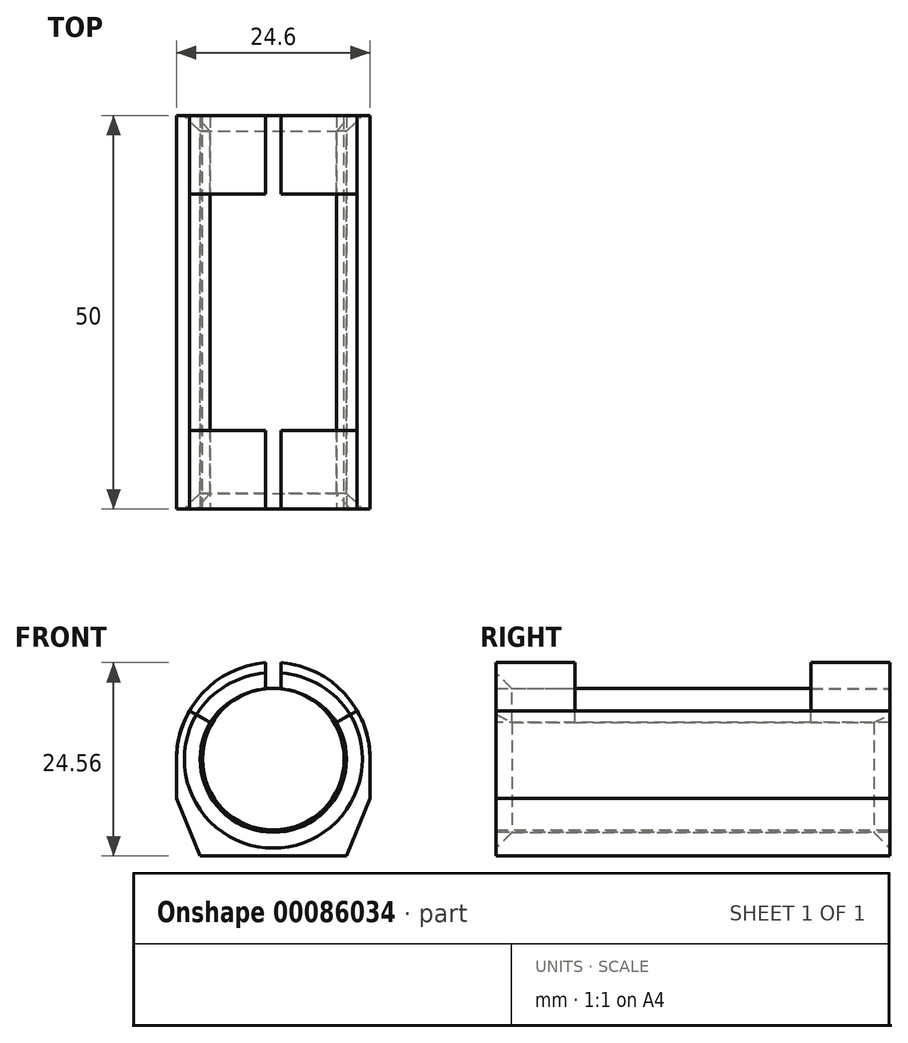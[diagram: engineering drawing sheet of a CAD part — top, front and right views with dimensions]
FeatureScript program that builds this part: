
annotation { "Feature Type Name" : "Feature", "Feature Type Description" : "" }
export const myFeature = defineFeature(function(context is Context, id is Id, definition is map)
    precondition{}
    {
        {
            var Q0;
            Q0=qCreatedBy(makeId("Front.planeOp"),FACE);
            var sketch = newSketch(context, id + "F0", { "sketchPlane" : qUnion([Q0])});
            skCircle(sketch, "E0", {"center": v(0, 0) * mm, "radius": 9 * mm});
            skSolve(sketch);
        }
        {
            var Q0;
            Q0 = qSketchRegion(id + "F0", true);
            extrude(context, id + "F1", {"entities" : qUnion([Q0]), "endBound" : BoundingType.SYMMETRIC, "depth" : 50 * mm});
        }
        {
            var Q0;
            Q0=qCreatedBy(makeId("Front.planeOp"),FACE);
            var sketch = newSketch(context, id + "F2", { "sketchPlane" : qUnion([Q0])});
            skCircle(sketch, "E1.0", {"center": v(0, 0) * mm, "radius": 9.3 * mm});
            skCircle(sketch, "E2.0", {"center": v(0, 0) * mm, "radius": 12.3 * mm});
            skLineSegment(sketch, "E3.bottom", {"start": v(-12.3, 0) * mm, "end": v(12.3, 0) * mm});
            skLineSegment(sketch, "E3.top", {"start": v(-12.3, -12.3) * mm, "end": v(12.3, -12.3) * mm});
            skLineSegment(sketch, "E3.left", {"start": v(-12.3, 0) * mm, "end": v(-12.3, -12.3) * mm});
            skLineSegment(sketch, "E3.right", {"start": v(12.3, 0) * mm, "end": v(12.3, -12.3) * mm});
            skLineSegment(sketch, "E4", {"start": v(0, 0) * mm, "end": v(-10.65, 6.15) * mm});
            skLineSegment(sketch, "E5", {"start": v(0, 0) * mm, "end": v(10.65, 6.15) * mm});
            skSolve(sketch);
        }
        {
            var Q0;
            {var subQ0=sQuery(id+"F2.wireOp",EDGE,"E3.right");Q0=makeQuery(id+"F2.imprint","IMPRINT",FACE,{"disambiguationData":[TD([[makeQuery(id+"F2.imprint","IMPRINT",EDGE,{"derivedFrom":subQ0}),-1.0]])]});}
            var Q1;
            {var subQ0=sQuery(id+"F2.wireOp",EDGE,"E3.left");Q1=makeQuery(id+"F2.imprint","IMPRINT",FACE,{"disambiguationData":[TD([[makeQuery(id+"F2.imprint","IMPRINT",EDGE,{"derivedFrom":subQ0}),1.0]])]});}
            var Q2;
            {var subQ0=sQuery(id+"F2.wireOp",EDGE,"E3.bottom");var subQ4=sQuery(id+"F2.wireOp",EDGE,"E1.0");var subQ7=makeQuery(id+"F2.imprint","INTERSECT",VERTEX,{"disambiguationData":[OD(0.0)],"derivedFrom":[subQ4,subQ0]});Q2=makeQuery(id+"F2.imprint","IMPRINT",FACE,{"disambiguationData":[TD([[makeQuery(id+"F2.imprint","IMPRINT",EDGE,{"disambiguationData":[TD([[subQ7,1.0]])],"derivedFrom":subQ4}),-1.0]])]});}
            var Q3;
            {var subQ0=sQuery(id+"F2.wireOp",EDGE,"E4");var subQ1=sQuery(id+"F2.wireOp",EDGE,"E1.0");var subQ2=makeQuery(id+"F2.imprint","INTERSECT",VERTEX,{"derivedFrom":[subQ1,subQ0]});Q3=makeQuery(id+"F2.imprint","IMPRINT",FACE,{"disambiguationData":[TD([[makeQuery(id+"F2.imprint","IMPRINT",EDGE,{"disambiguationData":[TD([[subQ2,-1.0]])],"derivedFrom":subQ1}),-1.0]])]});}
            var Q4;
            {var subQ0=sQuery(id+"F2.wireOp",EDGE,"E5");var subQ1=sQuery(id+"F2.wireOp",EDGE,"E1.0");var subQ2=makeQuery(id+"F2.imprint","INTERSECT",VERTEX,{"derivedFrom":[subQ1,subQ0]});Q4=makeQuery(id+"F2.imprint","IMPRINT",FACE,{"disambiguationData":[TD([[makeQuery(id+"F2.imprint","IMPRINT",EDGE,{"disambiguationData":[TD([[subQ2,1.0]])],"derivedFrom":subQ1}),-1.0]])]});}
            extrude(context, id + "F3", {"entities" : qUnion([Q0, Q1, Q2, Q3, Q4]), "endBound" : BoundingType.SYMMETRIC, "depth" : 50 * mm});
        }
        {
            var Q0;
            Q0=makeQuery(id+"F3.opExtrude","CAP_FACE",FACE,{"disambiguationData":[OSD([sQuery(id+"F2.wireOp",EDGE,"E1.0"),sQuery(id+"F2.wireOp",EDGE,"E2.0"),sQuery(id+"F2.wireOp",EDGE,"E3.top"),sQuery(id+"F2.wireOp",EDGE,"E3.left"),sQuery(id+"F2.wireOp",EDGE,"E3.right"),sQuery(id+"F2.wireOp",EDGE,"E4"),sQuery(id+"F2.wireOp",EDGE,"E5")])],"isStart":false});
            var sketch = newSketch(context, id + "F4", { "sketchPlane" : qUnion([Q0])});
            skCircle(sketch, "E6", {"center": v(0, 0) * mm, "radius": 9.3 * mm});
            skCircle(sketch, "E7", {"center": v(0, 0) * mm, "radius": 12.3 * mm});
            skLineSegment(sketch, "E8", {"start": v(-1, 8.95) * mm, "end": v(-1, 12.26) * mm});
            skLineSegment(sketch, "E9", {"start": v(1, 12.26) * mm, "end": v(1, 8.94) * mm});
            skArc(sketch, "E10", {"start": v(0, 9) * mm, "mid": v(-4.58, 7.84) * mm, "end": v(-8.05, 4.65) * mm});
            skArc(sketch, "E11.MirrorCS", {"start": v(0, 9) * mm, "mid": v(4.58, 7.84) * mm, "end": v(8.05, 4.65) * mm});
            skSolve(sketch);
        }
        {
            var Q0;
            {var subQ1=makeQuery(id+"F3.opExtrude","CAP_EDGE",EDGE,{"disambiguationData":[OSD([sQuery(id+"F2.wireOp",EDGE,"E5")])],"isStart":false});Q0=makeQuery(id+"F4.imprint","IMPRINT",FACE,{"disambiguationData":[TD([[makeQuery(id+"F4.imprint","IMPRINT",EDGE,{"derivedFrom":subQ1}),1.0]])]});}
            var Q1;
            {var subQ1=makeQuery(id+"F3.opExtrude","CAP_EDGE",EDGE,{"disambiguationData":[OSD([sQuery(id+"F2.wireOp",EDGE,"E4")])],"isStart":false});Q1=makeQuery(id+"F4.imprint","IMPRINT",FACE,{"disambiguationData":[TD([[makeQuery(id+"F4.imprint","IMPRINT",EDGE,{"derivedFrom":subQ1}),-1.0]])]});}
            var Q2;
            {var subQ0=sQuery(id+"F4.wireOp",EDGE,"E10");var subQ3=sQuery(id+"F4.wireOp",EDGE,"E8");var subQ5=makeQuery(id+"F4.imprint","INTERSECT",VERTEX,{"derivedFrom":[subQ3,subQ0]});Q2=makeQuery(id+"F4.imprint","IMPRINT",FACE,{"disambiguationData":[TD([[makeQuery(id+"F4.imprint","IMPRINT",EDGE,{"disambiguationData":[TD([[subQ5,-1.0]])],"derivedFrom":subQ3}),1.0]])]});}
            var Q3;
            {var subQ0=sQuery(id+"F4.wireOp",EDGE,"E11.MirrorCS");var subQ3=sQuery(id+"F4.wireOp",EDGE,"E9");var subQ5=makeQuery(id+"F4.imprint","INTERSECT",VERTEX,{"derivedFrom":[subQ3,subQ0]});Q3=makeQuery(id+"F4.imprint","IMPRINT",FACE,{"disambiguationData":[TD([[makeQuery(id+"F4.imprint","IMPRINT",EDGE,{"disambiguationData":[TD([[subQ5,1.0]])],"derivedFrom":subQ3}),1.0]])]});}
            extrude(context, id + "F5", {"entities" : qUnion([Q0, Q1, Q2, Q3]), "operationType" : NewBodyOperationType.ADD, "oppositeDirection" : true, "depth" : 10 * mm});
        }
        {
            var Q0;
            Q0=makeQuery(id+"F3.opExtrude","SWEPT_BODY",BODY,{"disambiguationData":[OSD([sQuery(id+"F2.wireOp",EDGE,"E1.0"),sQuery(id+"F2.wireOp",EDGE,"E2.0"),sQuery(id+"F2.wireOp",EDGE,"E3.top"),sQuery(id+"F2.wireOp",EDGE,"E3.left"),sQuery(id+"F2.wireOp",EDGE,"E3.right"),sQuery(id+"F2.wireOp",EDGE,"E4"),sQuery(id+"F2.wireOp",EDGE,"E5")])]});
            var Q1;
            Q1=qCreatedBy(makeId("Front.planeOp"),FACE);
            mirror(context, id + "F6", {"operationType" : NewBodyOperationType.ADD, "entities" : qUnion([Q0]), "mirrorPlane" : qUnion([Q1])});
        }
        {
            var Q0;
            {var subQ0=sQuery(id+"F4.wireOp",EDGE,"E7");var subQ1=sQuery(id+"F2.wireOp",EDGE,"E4");var subQ2=sQuery(id+"F2.wireOp",EDGE,"E5");Q0=makeQuery(id+"F5.boolean.opBoolean","MERGE",FACE,{"derivedFrom":[makeQuery(id+"F3.opExtrude","CAP_FACE",FACE,{"disambiguationData":[OSD([sQuery(id+"F2.wireOp",EDGE,"E1.0"),sQuery(id+"F2.wireOp",EDGE,"E2.0"),sQuery(id+"F2.wireOp",EDGE,"E3.top"),sQuery(id+"F2.wireOp",EDGE,"E3.left"),sQuery(id+"F2.wireOp",EDGE,"E3.right"),subQ1,subQ2])],"isStart":false}),makeQuery(id+"F5.opExtrude","CAP_FACE",FACE,{"disambiguationData":[OSD([subQ2,subQ0,sQuery(id+"F4.wireOp",EDGE,"E9"),sQuery(id+"F4.wireOp",EDGE,"E11.MirrorCS")])],"isStart":true}),makeQuery(id+"F5.opExtrude","CAP_FACE",FACE,{"disambiguationData":[OSD([subQ1,subQ0,sQuery(id+"F4.wireOp",EDGE,"E8"),sQuery(id+"F4.wireOp",EDGE,"E10")])],"isStart":true})]});}
            var sketch = newSketch(context, id + "F7", { "sketchPlane" : qUnion([Q0])});
            skLineSegment(sketch, "E12", {"start": v(-12.3, -5) * mm, "end": v(-9.3, -12.3) * mm});
            skLineSegment(sketch, "E13", {"start": v(9.3, -12.3) * mm, "end": v(12.3, -5) * mm});
            skLineSegment(sketch, "E14", {"start": v(-12.3, -5) * mm, "end": v(-12.3, -12.3) * mm});
            skLineSegment(sketch, "E15", {"start": v(-12.3, -12.3) * mm, "end": v(-9.3, -12.3) * mm});
            skLineSegment(sketch, "E16", {"start": v(9.3, -12.3) * mm, "end": v(12.3, -12.3) * mm});
            skLineSegment(sketch, "E17", {"start": v(12.3, -12.3) * mm, "end": v(12.3, -5) * mm});
            skLineSegment(sketch, "E18", {"start": v(-12.3, 0) * mm, "end": v(-12.3, -5) * mm, "construction": true});
            skSolve(sketch);
        }
        {
            var Q0;
            Q0 = qSketchRegion(id + "F7", true);
            extrude(context, id + "F8", {"entities" : qUnion([Q0]), "operationType" : NewBodyOperationType.REMOVE, "endBound" : BoundingType.THROUGH_ALL, "oppositeDirection" : true, "depth" : 25 * mm});
        }
        {
            var Q0;
            Q0=makeQuery(id+"F3.opExtrude","CAP_EDGE",EDGE,{"disambiguationData":[OSD([sQuery(id+"F2.wireOp",EDGE,"E1.0")])],"isStart":false});
            var Q1;
            Q1=makeQuery(id+"F5.opExtrude","CAP_EDGE",EDGE,{"disambiguationData":[OSD([sQuery(id+"F4.wireOp",EDGE,"E10")])],"isStart":true});
            var Q2;
            Q2=makeQuery(id+"F5.opExtrude","CAP_EDGE",EDGE,{"disambiguationData":[OSD([sQuery(id+"F4.wireOp",EDGE,"E11.MirrorCS")])],"isStart":true});
            var Q3;
            Q3=makeQuery(id+"F3.opExtrude","CAP_EDGE",EDGE,{"disambiguationData":[OSD([sQuery(id+"F2.wireOp",EDGE,"E1.0")])],"isStart":true});
            chamfer(context, id + "F9", {"entities" : qUnion([Q0, Q1, Q2, Q3]), "width" : 2 * mm, "tangentPropagation" : true});
        }
    });
